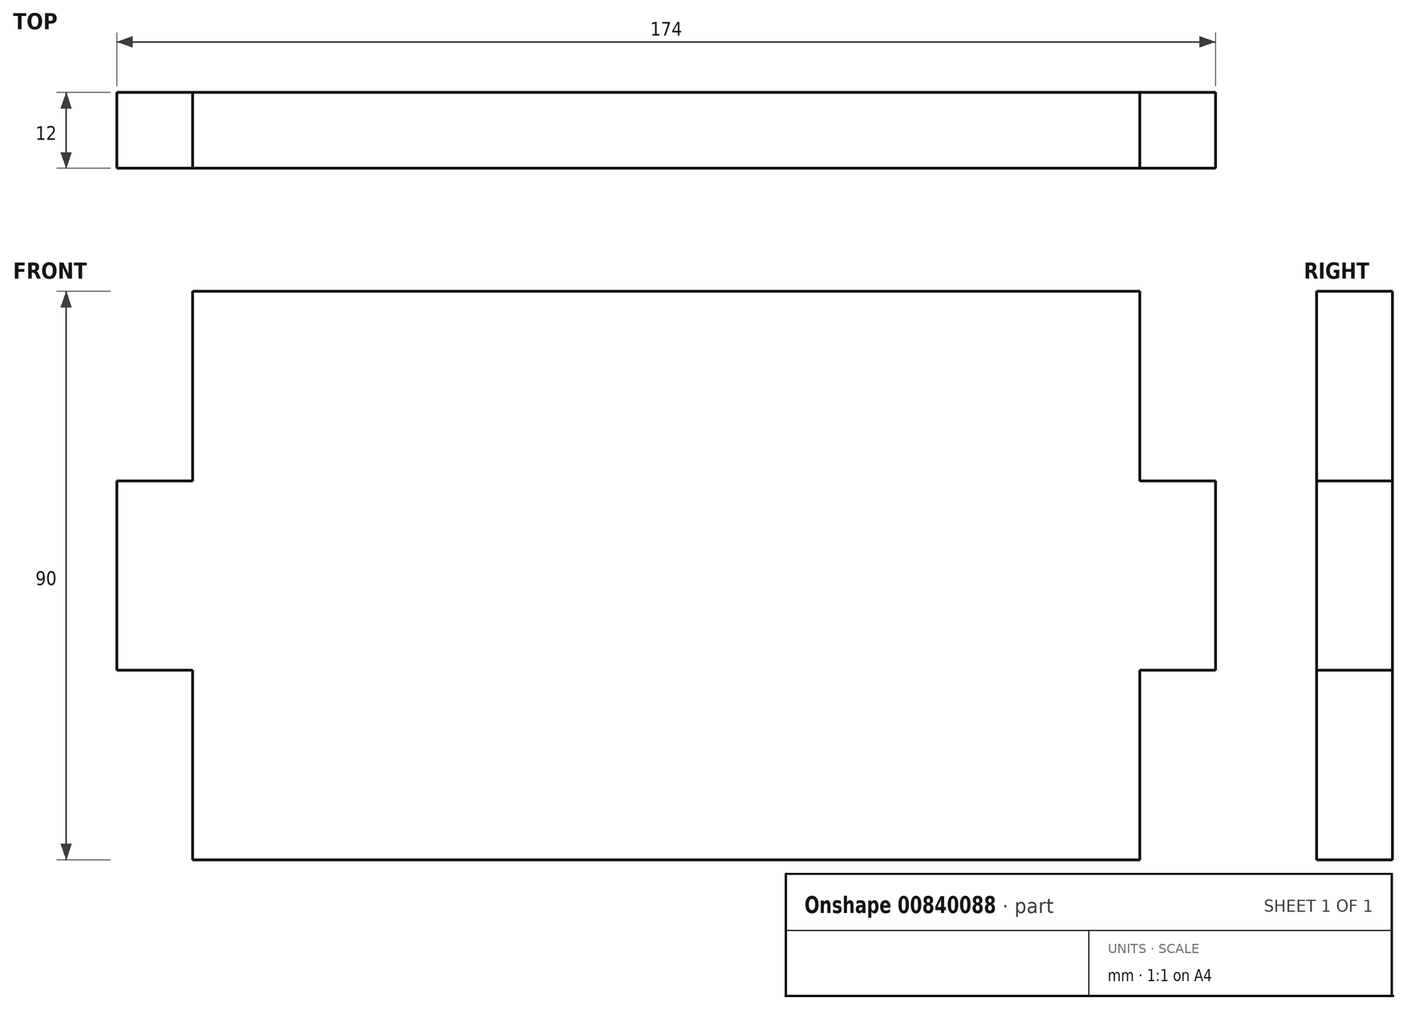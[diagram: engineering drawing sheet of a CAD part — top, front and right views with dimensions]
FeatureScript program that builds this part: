
annotation { "Feature Type Name" : "Feature", "Feature Type Description" : "" }
export const myFeature = defineFeature(function(context is Context, id is Id, definition is map)
    precondition{}
    {
        {
            var Q0;
            Q0=qCreatedBy(makeId("Front.planeOp"),FACE);
            var sketch = newSketch(context, id + "F0", { "sketchPlane" : qUnion([Q0])});
            skLineSegment(sketch, "E0", {"start": v(0, 0) * mm, "end": v(0, 30) * mm});
            skLineSegment(sketch, "E1", {"start": v(0, 30) * mm, "end": v(12, 30) * mm});
            skLineSegment(sketch, "E2", {"start": v(12, 30) * mm, "end": v(12, 60) * mm});
            skLineSegment(sketch, "E3", {"start": v(12, 60) * mm, "end": v(87, 60) * mm});
            skLineSegment(sketch, "E4", {"start": v(0, 0) * mm, "end": v(12, 0) * mm});
            skLineSegment(sketch, "E5", {"start": v(12, 0) * mm, "end": v(12, -30) * mm});
            skLineSegment(sketch, "E6", {"start": v(12, -30) * mm, "end": v(87, -30) * mm});
            skLineSegment(sketch, "E7", {"start": v(87, 60) * mm, "end": v(87, -30) * mm, "construction": true});
            skLineSegment(sketch, "E8.MirrorCS", {"start": v(162, 60) * mm, "end": v(87, 60) * mm});
            skLineSegment(sketch, "E9.MirrorCS", {"start": v(162, 30) * mm, "end": v(162, 60) * mm});
            skLineSegment(sketch, "E10.MirrorCS", {"start": v(174, 30) * mm, "end": v(162, 30) * mm});
            skLineSegment(sketch, "E11.MirrorCS", {"start": v(174, 0) * mm, "end": v(174, 30) * mm});
            skLineSegment(sketch, "E12.MirrorCS", {"start": v(174, 0) * mm, "end": v(162, 0) * mm});
            skLineSegment(sketch, "E13.MirrorCS", {"start": v(162, 0) * mm, "end": v(162, -30) * mm});
            skLineSegment(sketch, "E14.MirrorCS", {"start": v(162, -30) * mm, "end": v(87, -30) * mm});
            skSolve(sketch);
        }
        {
            var Q0;
            Q0 = qSketchRegion(id + "F0", true);
            extrude(context, id + "F1", {"entities" : qUnion([Q0]), "depth" : 12 * mm, "offsetDistance" : 25 * mm});
        }
    });
